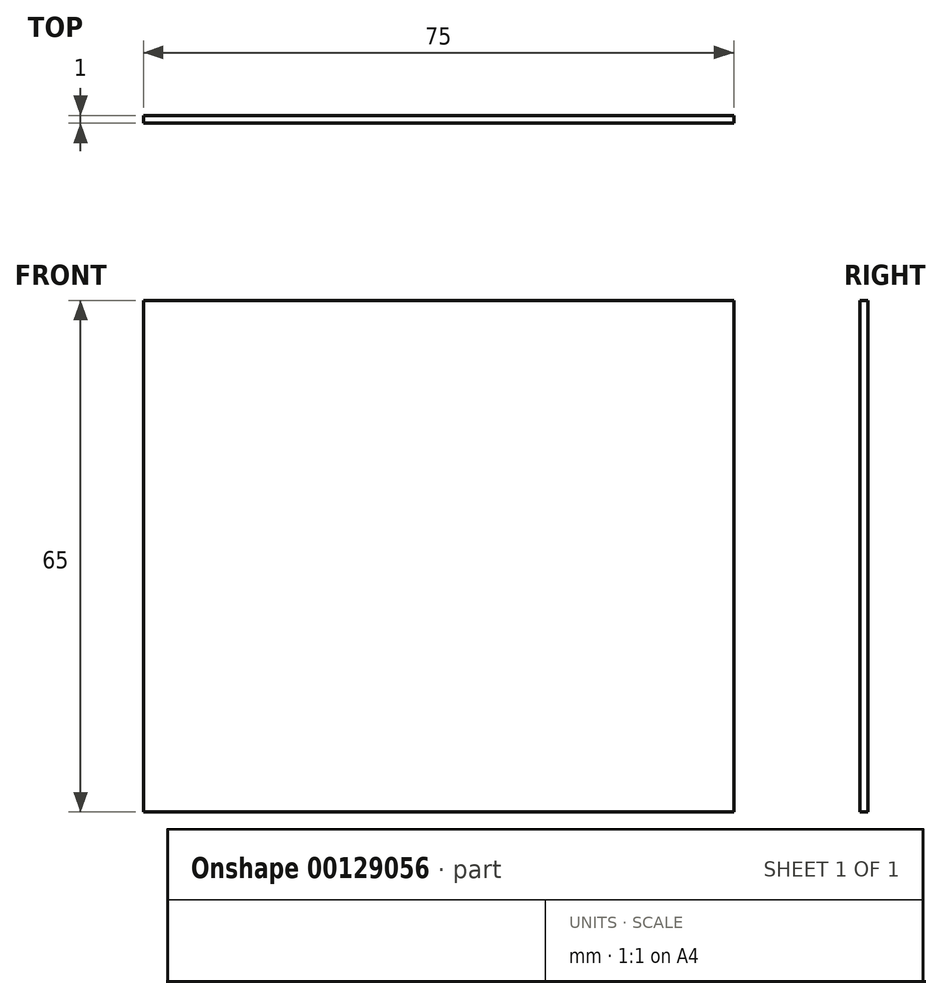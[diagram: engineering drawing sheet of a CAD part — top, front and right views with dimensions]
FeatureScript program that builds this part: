
annotation { "Feature Type Name" : "Feature", "Feature Type Description" : "" }
export const myFeature = defineFeature(function(context is Context, id is Id, definition is map)
    precondition{}
    {
        {
            var Q0;
            Q0=qCreatedBy(makeId("Front.planeOp"),FACE);
            var sketch = newSketch(context, id + "F0", { "sketchPlane" : qUnion([Q0])});
            skLineSegment(sketch, "E0.bottom", {"start": v(0, 0) * mm, "end": v(75, 0) * mm});
            skLineSegment(sketch, "E0.top", {"start": v(0, 65) * mm, "end": v(75, 65) * mm});
            skLineSegment(sketch, "E0.left", {"start": v(0, 0) * mm, "end": v(0, 65) * mm});
            skLineSegment(sketch, "E0.right", {"start": v(75, 0) * mm, "end": v(75, 65) * mm});
            skSolve(sketch);
        }
        {
            var Q0;
            Q0=makeQuery(id+"F0.imprint","IMPRINT",FACE,{"disambiguationData":[TD([[makeQuery(id+"F0.imprint","IMPRINT",EDGE,{"derivedFrom":sQuery(id+"F0.wireOp",EDGE,"E0.bottom")}),1.0]])]});
            extrude(context, id + "F1", {"entities" : qUnion([Q0]), "depth" : 1 * mm});
        }
    });
